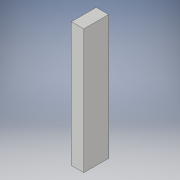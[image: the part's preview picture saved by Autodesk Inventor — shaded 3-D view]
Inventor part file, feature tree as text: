
AUTODESK INVENTOR PART (.ipt)
format: ipt  version: 2017 (Build 210142000, 142)  size: 90,112 bytes
history: native  units: in
note: dims shown in document units (in); Inventor stores cm internally (conversion verified against a paired STEP export)
features: extrude x1, sketch x1
ambient origin geometry x8: Origin, YZ Plane, XZ Plane, XY Plane, X Axis, Y Axis, Z Axis, Center Point
bodies: Solid1 (feature_tree)
feature tree (2):
  extrude  "Extrusion1"  Depth=1.5in
  sketch  "Sketch1"  dims[d0=0.75in d1=1.5in d2=7.5in d3=0.0in]
